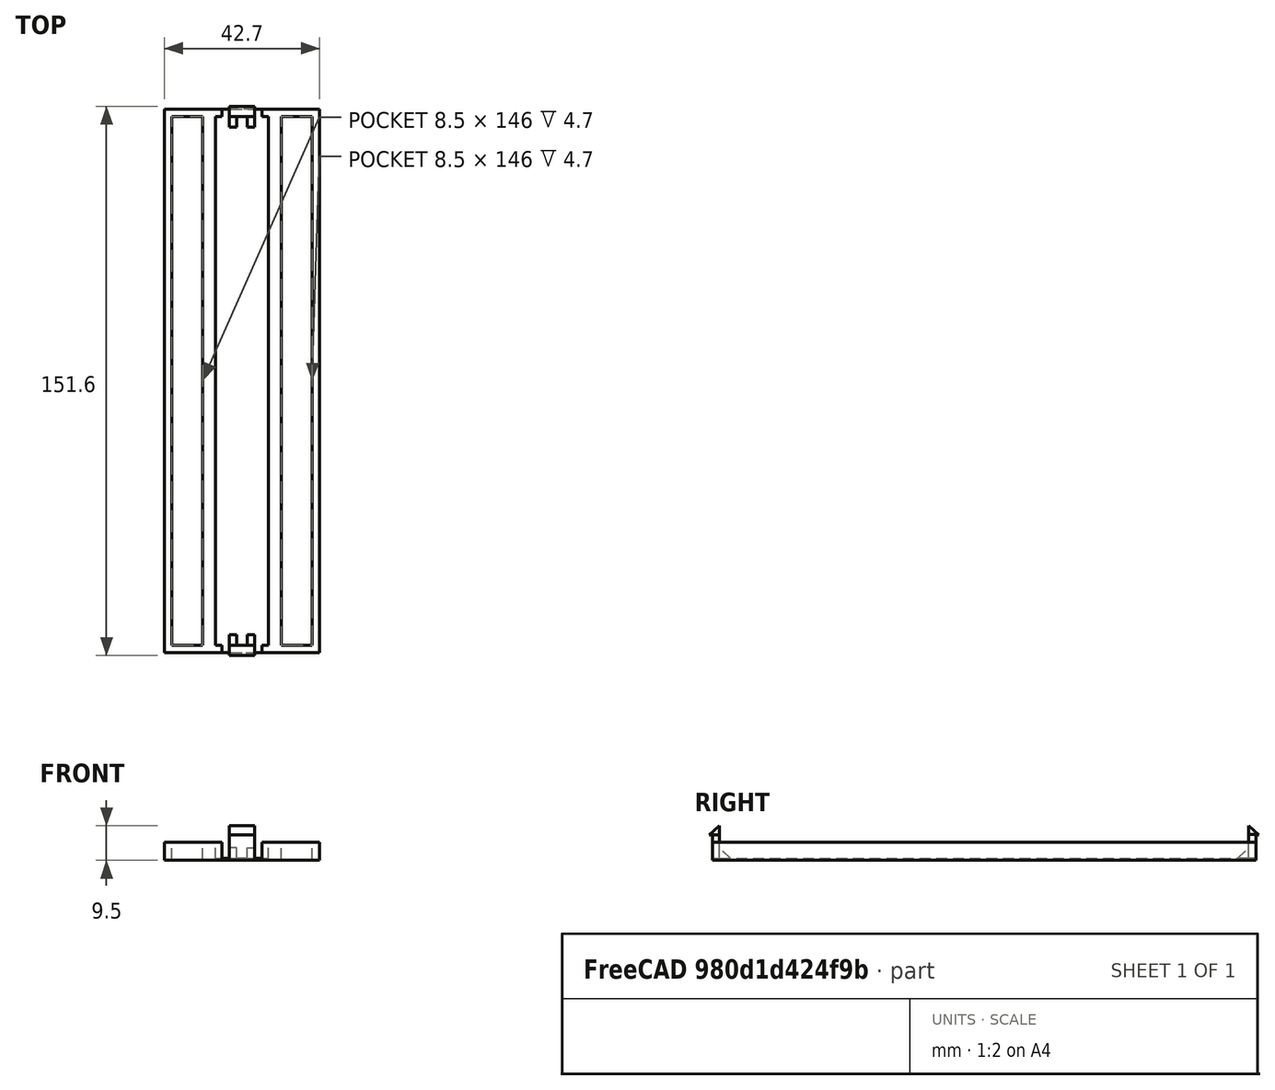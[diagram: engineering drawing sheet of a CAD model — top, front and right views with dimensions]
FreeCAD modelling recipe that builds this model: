
FCSTD DOCUMENT  (FreeCAD 0.14R2935 (Git))
Label: plastic_part_PcBox
License: CC-BY 3.0
LicenseURL: http://creativecommons.org/licenses/by/3.0/
objects: Part::Box×13, Part::MultiFuse×6, Part::Cut×5
note: 24 computed .brp shape members not serialized (recipe doc carries the construction recipe); baked Part::Feature solids carry a one-line shape summary decoded from their .brp

FEATURE [Part::Box] Box  label="Rect_Body"
  Height = 5
  Length = 42.7
  Width = 150
FEATURE [Part::Box] Box001  label="Rectangulo_Body_cut-right"
  Height = 4.7
  Length = 8.5
  Placement = pos=(32.2,2,0.3) rot=(0,0,1;0rad)
  Width = 146
FEATURE [Part::Box] Box002  label="Rectangulo_Body_cut-center"
  Height = 4.5
  Length = 14.7
  Placement = pos=(14,2,0.5) rot=(0,0,1;0rad)
  Width = 146
FEATURE [Part::Box] Box003  label="Rect_Base_left-cut"
  Height = 4.7
  Length = 8.5
  Placement = pos=(2,2,0.3) rot=(0,0,1;0rad)
  Width = 146
FEATURE [Part::Box] Box004  label="Rect_Base_center-cut_border"
  Height = 4.5
  Length = 11
  Placement = pos=(15.85,0,0.5) rot=(0,0,1;0rad)
  Width = 150
FEATURE [Part::MultiFuse] Fusion  label="Rect_Recorte"
  Shapes = -> [Box004,Box003,Box002,Box001]
FEATURE [Part::Cut] Cut  label="PcBox_without_Clip"
  Base = -> Box
  Tool = -> Fusion
FEATURE [Part::Box] Box005  label="Clip_body"
  Height = 6.7
  Length = 7
  Placement = pos=(17.85,0,0.5) rot=(0,0,1;0rad)
  Width = 2
FEATURE [Part::Box] Box006  label="Pestaña_inferior_cabezal_base"
  Height = 2.5
  Length = 7
  Placement = pos=(17.85,-0.8,7) rot=(0,0,1;0rad)
  Width = 2.8
FEATURE [Part::Box] Box007  label="Pestaña_inferior_cabezal_recorte"
  Height = 4.5
  Length = 9
  Placement = pos=(16.85,-3.22,8.59) rot=(-1,0,0;0.841946rad)
  Width = 2.8
FEATURE [Part::Cut] Cut001  label="Clip_head"
  Base = -> Box006
  Tool = -> Box007
FEATURE [Part::Box] Box010  label="Refuerzo_Base"
  Height = 3
  Length = 2
  Width = 3
FEATURE [Part::Box] Box011  label="Refuerzo_Recorte"
  Height = 5
  Length = 2
  Placement = pos=(0,3.53553,-0.535534) rot=(1,0,0;0.785397rad)
  Width = 3
FEATURE [Part::Cut] Cut002  label="refuerzo_left"
  Base = -> Box010
  Tool = -> Box011
FEATURE [Part::Box] Box012  label="Refuerzo_Recorte001"
  Height = 5
  Length = 2
  Placement = pos=(0,3.53553,-0.535534) rot=(1,0,0;0.785397rad)
  Width = 3
FEATURE [Part::Box] Box013  label="Refuerzo_Base001"
  Height = 3
  Length = 2
  Width = 3
FEATURE [Part::Cut] Cut003  label="refuerzo_right"
  Base = -> Box013
  Placement = pos=(5,0,0) rot=(0,0,1;0rad)
  Tool = -> Box012
FEATURE [Part::MultiFuse] Fusion001  label="Refuerzo"
  Placement = pos=(17.85,2,0.5) rot=(0,0,1;0rad)
  Shapes = -> [Cut002,Cut003]
FEATURE [Part::MultiFuse] Fusion002  label="Clip_2"
  Shapes = -> [Box005,Cut001,Fusion001]
FEATURE [Part::MultiFuse] Fusion003  label="Refuerzo001"
  Placement = pos=(17.85,2,0.5) rot=(0,0,1;0rad)
  Shapes = -> [Cut002,Cut003]
FEATURE [Part::Cut] Cut004  label="Clip_head001"
  Base = -> Box006
  Tool = -> Box007
FEATURE [Part::Box] Box014  label="Clip_body001"
  Height = 6.7
  Length = 7
  Placement = pos=(17.85,0,0.5) rot=(0,0,1;0rad)
  Width = 2
FEATURE [Part::MultiFuse] Fusion004  label="Clip_1"
  Placement = pos=(42.7,150,0) rot=(0,0,1;3.14159rad)
  Shapes = -> [Box014,Cut004,Fusion003]
FEATURE [Part::MultiFuse] Fusion005  label="PcBox_Part"
  Shapes = -> [Cut,Fusion004,Fusion002]
